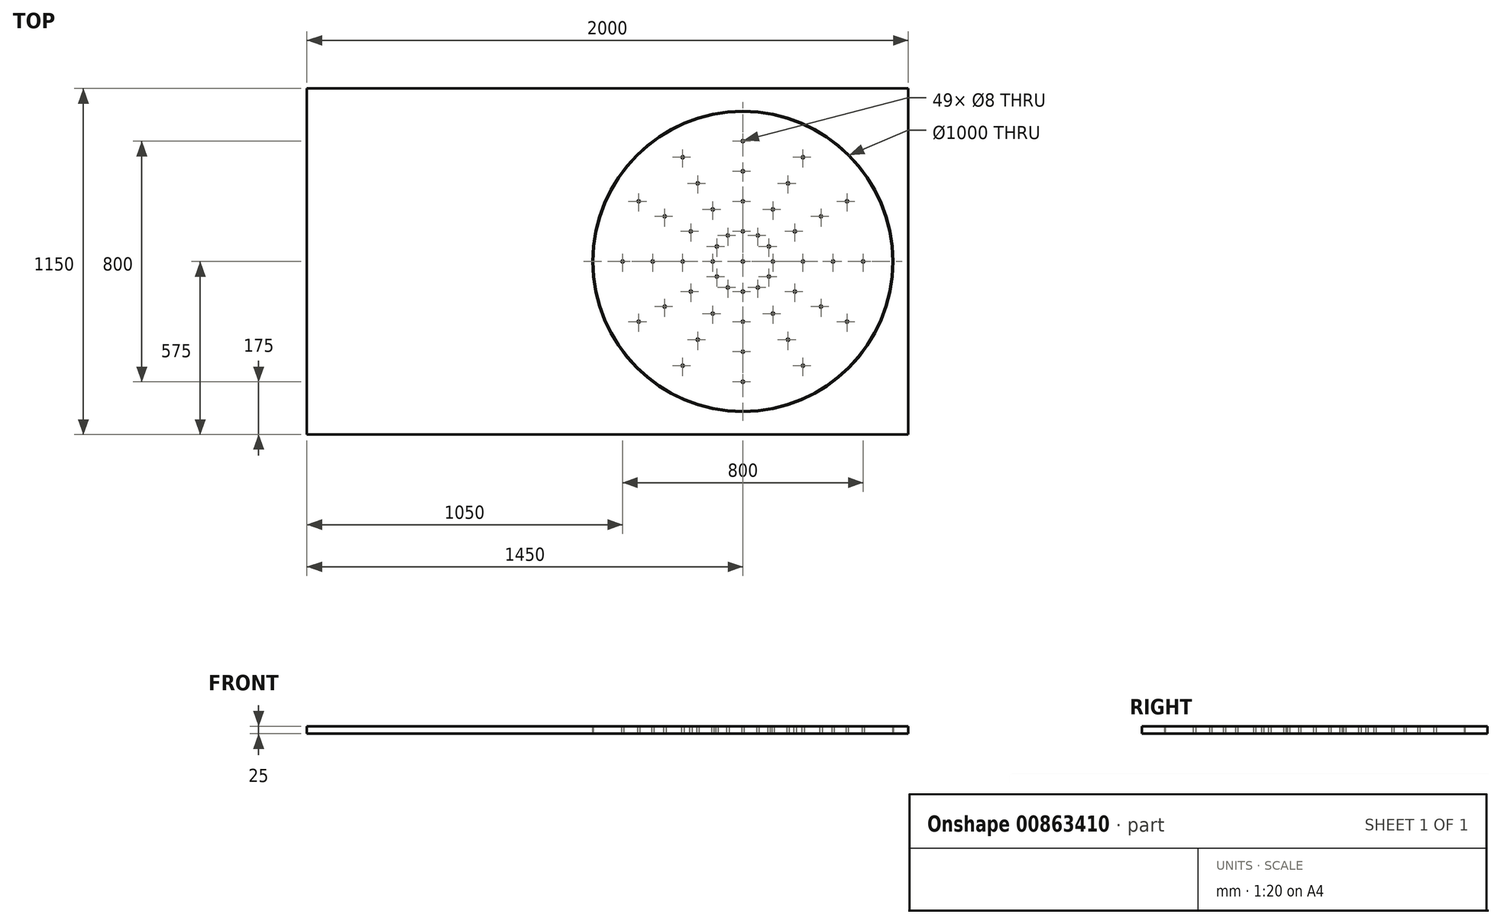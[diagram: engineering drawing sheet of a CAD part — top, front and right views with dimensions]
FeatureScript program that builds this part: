
annotation { "Feature Type Name" : "Feature", "Feature Type Description" : "" }
export const myFeature = defineFeature(function(context is Context, id is Id, definition is map)
    precondition{}
    {
        {
            var Q0;
            Q0=qCreatedBy(makeId("Top.planeOp"),FACE);
            var sketch = newSketch(context, id + "F0", { "sketchPlane" : qUnion([Q0])});
            skLineSegment(sketch, "E0.bottom", {"start": v(-1958.5, 1125.95) * mm, "end": v(41.5, 1125.95) * mm});
            skLineSegment(sketch, "E0.top", {"start": v(-1958.5, -24.05) * mm, "end": v(41.5, -24.05) * mm});
            skLineSegment(sketch, "E0.left", {"start": v(-1958.5, 1125.95) * mm, "end": v(-1958.5, -24.05) * mm});
            skLineSegment(sketch, "E0.right", {"start": v(41.5, 1125.95) * mm, "end": v(41.5, -24.05) * mm});
            skLineSegment(sketch, "E1", {"start": v(41.5, 550.95) * mm, "end": v(-508.5, 550.95) * mm, "construction": true});
            skCircle(sketch, "E2", {"center": v(-508.5, 550.95) * mm, "radius": 500 * mm});
            skSolve(sketch);
        }
        {
            var Q0;
            Q0=makeQuery(id+"F0.imprint","IMPRINT",FACE,{"disambiguationData":[TD([[makeQuery(id+"F0.imprint","IMPRINT",EDGE,{"derivedFrom":sQuery(id+"F0.wireOp",EDGE,"E0.bottom")}),-1.0]])]});
            extrude(context, id + "F1", {"entities" : qUnion([Q0]), "depth" : 25 * mm, "offsetDistance" : 25 * mm});
        }
        {
            var Q0;
            Q0=makeQuery(id+"F0.imprint","IMPRINT",FACE,{"disambiguationData":[TD([[makeQuery(id+"F0.imprint","IMPRINT",EDGE,{"derivedFrom":sQuery(id+"F0.wireOp",EDGE,"E2")}),1.0]])]});
            var sketch = newSketch(context, id + "F2", { "sketchPlane" : qUnion([Q0])});
            skCircle(sketch, "E3", {"center": v(-508.5, 550.95) * mm, "radius": 497.5 * mm});
            skLineSegment(sketch, "E4", {"start": v(-508.5, 550.95) * mm, "end": v(-508.5, 450.95) * mm, "construction": true});
            skLineSegment(sketch, "E5", {"start": v(-508.5, 450.95) * mm, "end": v(-508.5, 350.95) * mm, "construction": true});
            skLineSegment(sketch, "E6", {"start": v(-508.5, 350.95) * mm, "end": v(-508.5, 250.95) * mm, "construction": true});
            skLineSegment(sketch, "E7", {"start": v(-508.5, 250.95) * mm, "end": v(-508.5, 150.95) * mm, "construction": true});
            skCircle(sketch, "E8", {"center": v(-508.5, 450.95) * mm, "radius": 4 * mm});
            skCircle(sketch, "E9", {"center": v(-508.5, 350.95) * mm, "radius": 4 * mm});
            skCircle(sketch, "E10", {"center": v(-508.5, 250.95) * mm, "radius": 4 * mm});
            skCircle(sketch, "E11", {"center": v(-508.5, 150.95) * mm, "radius": 4 * mm});
            skCircle(sketch, "E12.1.0", {"center": v(-458.5, 464.35) * mm, "radius": 4 * mm});
            skCircle(sketch, "E12.1.1", {"center": v(-408.5, 377.74) * mm, "radius": 4 * mm});
            skCircle(sketch, "E12.1.2", {"center": v(-358.5, 291.14) * mm, "radius": 4 * mm});
            skCircle(sketch, "E12.1.3", {"center": v(-308.5, 204.54) * mm, "radius": 4 * mm});
            skCircle(sketch, "E12.2.0", {"center": v(-421.9, 500.95) * mm, "radius": 4 * mm});
            skCircle(sketch, "E12.2.1", {"center": v(-335.3, 450.95) * mm, "radius": 4 * mm});
            skCircle(sketch, "E12.2.2", {"center": v(-248.7, 400.95) * mm, "radius": 4 * mm});
            skCircle(sketch, "E12.2.3", {"center": v(-162.09, 350.95) * mm, "radius": 4 * mm});
            skCircle(sketch, "E12.3.0", {"center": v(-408.5, 550.95) * mm, "radius": 4 * mm});
            skCircle(sketch, "E12.3.1", {"center": v(-308.5, 550.95) * mm, "radius": 4 * mm});
            skCircle(sketch, "E12.3.2", {"center": v(-208.5, 550.95) * mm, "radius": 4 * mm});
            skCircle(sketch, "E12.3.3", {"center": v(-108.5, 550.95) * mm, "radius": 4 * mm});
            skCircle(sketch, "E12.4.0", {"center": v(-421.9, 600.95) * mm, "radius": 4 * mm});
            skCircle(sketch, "E12.4.1", {"center": v(-335.3, 650.95) * mm, "radius": 4 * mm});
            skCircle(sketch, "E12.4.2", {"center": v(-248.7, 700.95) * mm, "radius": 4 * mm});
            skCircle(sketch, "E12.4.3", {"center": v(-162.09, 750.95) * mm, "radius": 4 * mm});
            skCircle(sketch, "E12.5.0", {"center": v(-458.5, 637.55) * mm, "radius": 4 * mm});
            skCircle(sketch, "E12.5.1", {"center": v(-408.5, 724.16) * mm, "radius": 4 * mm});
            skCircle(sketch, "E12.5.2", {"center": v(-358.5, 810.76) * mm, "radius": 4 * mm});
            skCircle(sketch, "E12.5.3", {"center": v(-308.5, 897.36) * mm, "radius": 4 * mm});
            skCircle(sketch, "E12.6.0", {"center": v(-508.5, 650.95) * mm, "radius": 4 * mm});
            skCircle(sketch, "E12.6.1", {"center": v(-508.5, 750.95) * mm, "radius": 4 * mm});
            skCircle(sketch, "E12.6.2", {"center": v(-508.5, 850.95) * mm, "radius": 4 * mm});
            skCircle(sketch, "E12.6.3", {"center": v(-508.5, 950.95) * mm, "radius": 4 * mm});
            skCircle(sketch, "E12.7.0", {"center": v(-558.5, 637.55) * mm, "radius": 4 * mm});
            skCircle(sketch, "E12.7.1", {"center": v(-608.5, 724.16) * mm, "radius": 4 * mm});
            skCircle(sketch, "E12.7.2", {"center": v(-658.5, 810.76) * mm, "radius": 4 * mm});
            skCircle(sketch, "E12.7.3", {"center": v(-708.5, 897.36) * mm, "radius": 4 * mm});
            skCircle(sketch, "E12.8.0", {"center": v(-595.1, 600.95) * mm, "radius": 4 * mm});
            skCircle(sketch, "E12.8.1", {"center": v(-681.7, 650.95) * mm, "radius": 4 * mm});
            skCircle(sketch, "E12.8.2", {"center": v(-768.3, 700.95) * mm, "radius": 4 * mm});
            skCircle(sketch, "E12.8.3", {"center": v(-854.9, 750.95) * mm, "radius": 4 * mm});
            skCircle(sketch, "E12.9.0", {"center": v(-608.5, 550.95) * mm, "radius": 4 * mm});
            skCircle(sketch, "E12.9.1", {"center": v(-708.5, 550.95) * mm, "radius": 4 * mm});
            skCircle(sketch, "E12.9.2", {"center": v(-808.5, 550.95) * mm, "radius": 4 * mm});
            skCircle(sketch, "E12.9.3", {"center": v(-908.5, 550.95) * mm, "radius": 4 * mm});
            skCircle(sketch, "E12.10.0", {"center": v(-595.1, 500.95) * mm, "radius": 4 * mm});
            skCircle(sketch, "E12.10.1", {"center": v(-681.7, 450.95) * mm, "radius": 4 * mm});
            skCircle(sketch, "E12.10.2", {"center": v(-768.3, 400.95) * mm, "radius": 4 * mm});
            skCircle(sketch, "E12.10.3", {"center": v(-854.9, 350.95) * mm, "radius": 4 * mm});
            skCircle(sketch, "E12.11.0", {"center": v(-558.5, 464.35) * mm, "radius": 4 * mm});
            skCircle(sketch, "E12.11.1", {"center": v(-608.5, 377.74) * mm, "radius": 4 * mm});
            skCircle(sketch, "E12.11.2", {"center": v(-658.5, 291.14) * mm, "radius": 4 * mm});
            skCircle(sketch, "E12.11.3", {"center": v(-708.5, 204.54) * mm, "radius": 4 * mm});
            skCircle(sketch, "E13", {"center": v(-508.5, 550.95) * mm, "radius": 4 * mm});
            skSolve(sketch);
        }
        {
            var Q0;
            Q0=makeQuery(id+"F2.imprint","IMPRINT",FACE,{"disambiguationData":[TD([[makeQuery(id+"F2.imprint","IMPRINT",EDGE,{"derivedFrom":sQuery(id+"F2.wireOp",EDGE,"E3")}),1.0]])]});
            var Q1;
            Q1=makeQuery(id+"F2.imprint","IMPRINT",FACE,{"disambiguationData":[TD([[makeQuery(id+"F2.imprint","IMPRINT",EDGE,{"derivedFrom":sQuery(id+"F2.wireOp",EDGE,"E3")}),1.0]])]});
            extrude(context, id + "F3", {"entities" : qUnion([Q0, Q1]), "depth" : 25 * mm, "offsetDistance" : 25 * mm});
        }
    });
